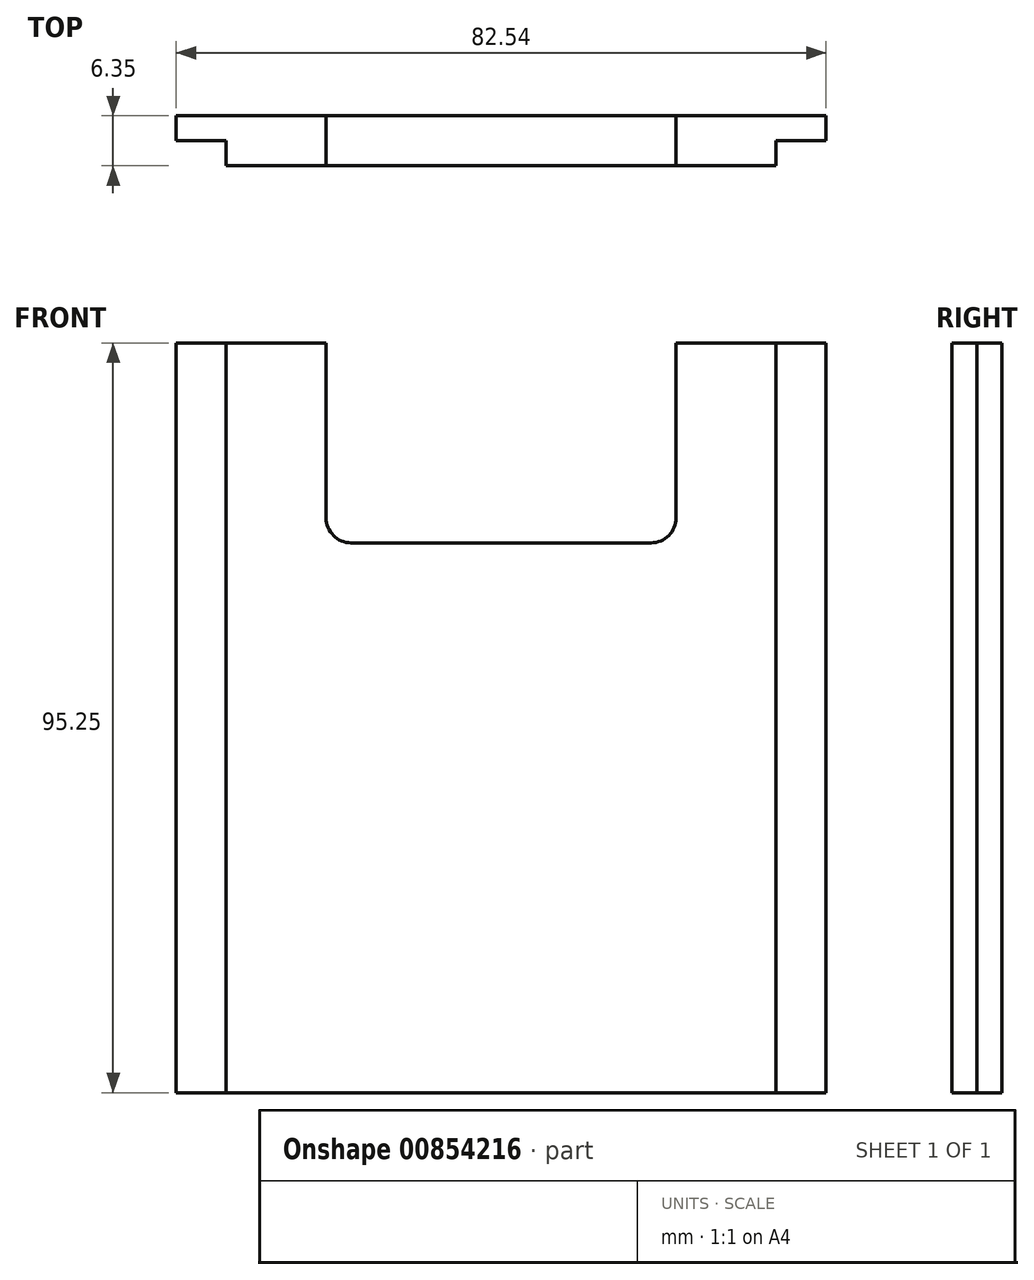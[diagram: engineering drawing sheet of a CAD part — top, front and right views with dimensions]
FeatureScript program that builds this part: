
annotation { "Feature Type Name" : "Feature", "Feature Type Description" : "" }
export const myFeature = defineFeature(function(context is Context, id is Id, definition is map)
    precondition{}
    {
        {
            var Q0;
            Q0=qCreatedBy(makeId("Front.planeOp"),FACE);
            var sketch = newSketch(context, id + "F0", { "sketchPlane" : qUnion([Q0])});
            skLineSegment(sketch, "E0", {"start": v(0, 0) * mm, "end": v(-41.28, 0) * mm});
            skLineSegment(sketch, "E1", {"start": v(0, 0) * mm, "end": v(41.28, 0) * mm});
            skLineSegment(sketch, "E2", {"start": v(41.28, 0) * mm, "end": v(41.27, 95.25) * mm});
            skLineSegment(sketch, "E3", {"start": v(-41.28, 0) * mm, "end": v(-41.28, 95.25) * mm});
            skLineSegment(sketch, "E4", {"start": v(-41.28, 95.25) * mm, "end": v(-22.23, 95.25) * mm});
            skLineSegment(sketch, "E5.top", {"start": v(-19.05, 69.85) * mm, "end": v(19.05, 69.85) * mm});
            skLineSegment(sketch, "E5.left", {"start": v(-22.23, 95.25) * mm, "end": v(-22.23, 73.02) * mm});
            skLineSegment(sketch, "E5.right", {"start": v(22.22, 95.25) * mm, "end": v(22.22, 73.02) * mm});
            skLineSegment(sketch, "E6.trimOffspring", {"start": v(22.22, 95.25) * mm, "end": v(41.28, 95.25) * mm});
            skPoint(sketch, "E7.visualSharp", {"position": v(22.22, 69.85) * mm});
            skPoint(sketch, "E8.visualSharp", {"position": v(-22.23, 69.85) * mm});
            skArc(sketch, "E9.filletArc", {"start": v(-22.23, 73.02) * mm, "mid": v(-21.3, 70.78) * mm, "end": v(-19.05, 69.85) * mm});
            skArc(sketch, "E10.filletArc", {"start": v(19.05, 69.85) * mm, "mid": v(21.3, 70.78) * mm, "end": v(22.23, 73.02) * mm});
            skSolve(sketch);
        }
        {
            var Q0;
            Q0=makeQuery(id+"F0.imprint","IMPRINT",FACE,{"disambiguationData":[TD([[makeQuery(id+"F0.imprint","IMPRINT",EDGE,{"derivedFrom":sQuery(id+"F0.wireOp",EDGE,"E0")}),-1.0]])]});
            extrude(context, id + "F1", {"entities" : qUnion([Q0]), "depth" : 6.35 * mm, "offsetDistance" : 25.4 * mm});
        }
        {
            var Q0;
            Q0=makeQuery(id+"F1.opExtrude","CAP_FACE",FACE,{"disambiguationData":[OSD([sQuery(id+"F0.wireOp",EDGE,"E0"),sQuery(id+"F0.wireOp",EDGE,"E1"),sQuery(id+"F0.wireOp",EDGE,"E2"),sQuery(id+"F0.wireOp",EDGE,"E3"),sQuery(id+"F0.wireOp",EDGE,"E4"),sQuery(id+"F0.wireOp",EDGE,"E5.top"),sQuery(id+"F0.wireOp",EDGE,"E5.left"),sQuery(id+"F0.wireOp",EDGE,"E5.right"),sQuery(id+"F0.wireOp",EDGE,"E6.trimOffspring"),sQuery(id+"F0.wireOp",EDGE,"E7.filletArc"),sQuery(id+"F0.wireOp",EDGE,"E8.filletArc")])],"isStart":false});
            var sketch = newSketch(context, id + "F2", { "sketchPlane" : qUnion([Q0])});
            skLineSegment(sketch, "E11", {"start": v(-34.93, 95.25) * mm, "end": v(-34.93, 0) * mm});
            skLineSegment(sketch, "E12", {"start": v(34.92, 95.25) * mm, "end": v(34.93, 0) * mm});
            skSolve(sketch);
        }
        {
            var Q0;
            {var subQ0=sQuery(id+"F2.wireOp",EDGE,"E11");Q0=makeQuery(id+"F2.imprint","IMPRINT",FACE,{"disambiguationData":[TD([[makeQuery(id+"F2.imprint","IMPRINT",EDGE,{"derivedFrom":subQ0}),-1.0]])]});}
            var Q1;
            {var subQ0=sQuery(id+"F2.wireOp",EDGE,"E12");Q1=makeQuery(id+"F2.imprint","IMPRINT",FACE,{"disambiguationData":[TD([[makeQuery(id+"F2.imprint","IMPRINT",EDGE,{"derivedFrom":subQ0}),1.0]])]});}
            extrude(context, id + "F3", {"entities" : qUnion([Q0, Q1]), "operationType" : NewBodyOperationType.REMOVE, "oppositeDirection" : true, "depth" : 3.17 * mm, "offsetDistance" : 25.4 * mm});
        }
    });
